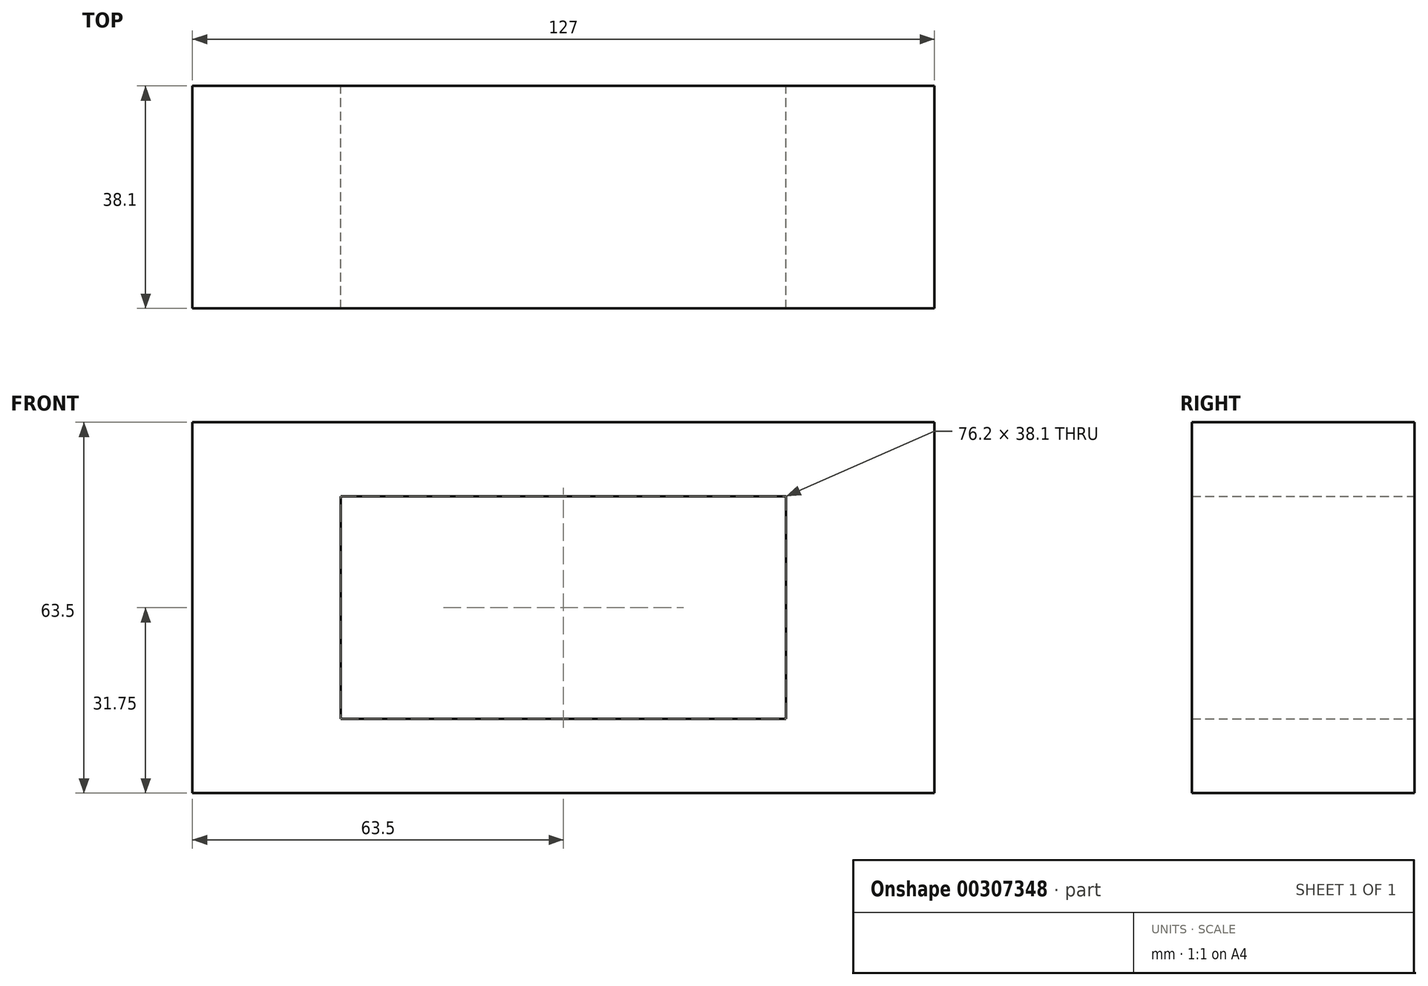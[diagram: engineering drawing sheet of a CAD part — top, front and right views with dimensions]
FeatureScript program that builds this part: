
annotation { "Feature Type Name" : "Feature", "Feature Type Description" : "" }
export const myFeature = defineFeature(function(context is Context, id is Id, definition is map)
    precondition{}
    {
        {
            var Q0;
            Q0=qCreatedBy(makeId("Front.planeOp"),FACE);
            var sketch = newSketch(context, id + "F0", { "sketchPlane" : qUnion([Q0])});
            skLineSegment(sketch, "E0.bottom", {"start": v(-63.5, 31.75) * mm, "end": v(63.5, 31.75) * mm});
            skLineSegment(sketch, "E0.top", {"start": v(-63.5, -31.75) * mm, "end": v(63.5, -31.75) * mm});
            skLineSegment(sketch, "E0.left", {"start": v(-63.5, 31.75) * mm, "end": v(-63.5, -31.75) * mm});
            skLineSegment(sketch, "E0.right", {"start": v(63.5, 31.75) * mm, "end": v(63.5, -31.75) * mm});
            skPoint(sketch, "E0.middle", {"position": v(0, 0) * mm});
            skLineSegment(sketch, "E1.bottom", {"start": v(-38.1, 19.05) * mm, "end": v(38.1, 19.05) * mm});
            skLineSegment(sketch, "E1.top", {"start": v(-38.1, -19.05) * mm, "end": v(38.1, -19.05) * mm});
            skLineSegment(sketch, "E1.left", {"start": v(-38.1, 19.05) * mm, "end": v(-38.1, -19.05) * mm});
            skLineSegment(sketch, "E1.right", {"start": v(38.1, 19.05) * mm, "end": v(38.1, -19.05) * mm});
            skSolve(sketch);
        }
        {
            var Q0;
            Q0 = qSketchRegion(id + "F0", true);
            extrude(context, id + "F1", {"entities" : qUnion([Q0]), "depth" : 38.1 * mm});
        }
    });
